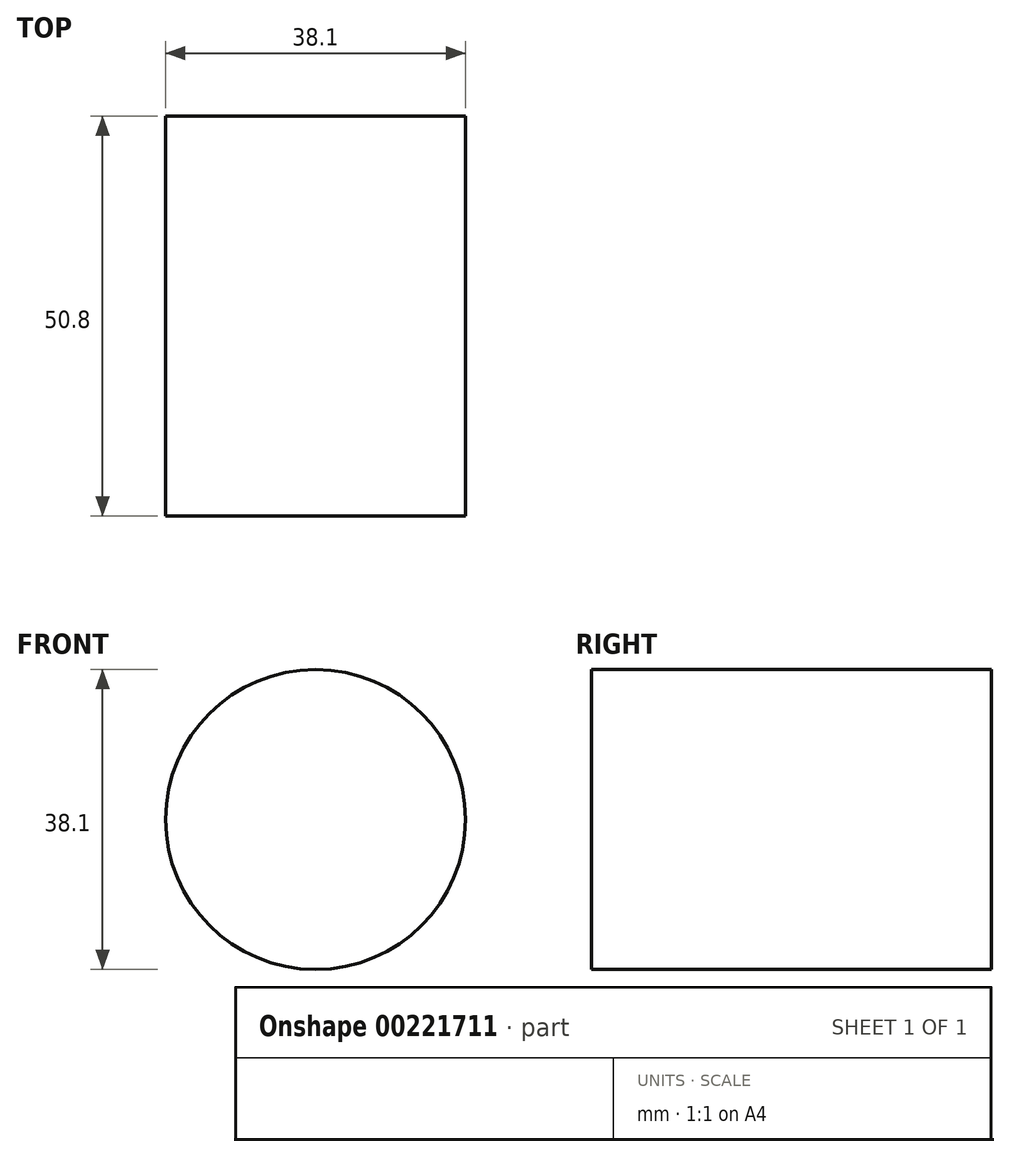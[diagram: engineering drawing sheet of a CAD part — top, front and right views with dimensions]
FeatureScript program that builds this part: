
annotation { "Feature Type Name" : "Feature", "Feature Type Description" : "" }
export const myFeature = defineFeature(function(context is Context, id is Id, definition is map)
    precondition{}
    {
        {
            var Q0;
            Q0=qCreatedBy(makeId("Front.planeOp"),FACE);
            var sketch = newSketch(context, id + "F0", { "sketchPlane" : qUnion([Q0])});
            skCircle(sketch, "E0", {"center": v(0, 0) * mm, "radius": 19.05 * mm});
            skCircle(sketch, "E1.0", {"center": v(0, 0) * mm, "radius": 12.7 * mm});
            skSolve(sketch);
        }
        {
            var Q0;
            Q0=makeQuery(id+"F0.imprint","IMPRINT",FACE,{"disambiguationData":[TD([[makeQuery(id+"F0.imprint","IMPRINT",EDGE,{"derivedFrom":sQuery(id+"F0.wireOp",EDGE,"E0")}),1.0]])]});
            var Q1;
            Q1=makeQuery(id+"F0.imprint","IMPRINT",FACE,{"disambiguationData":[TD([[makeQuery(id+"F0.imprint","IMPRINT",EDGE,{"derivedFrom":sQuery(id+"F0.wireOp",EDGE,"E1.0")}),1.0]])]});
            extrude(context, id + "F1", {"entities" : qUnion([Q0, Q1]), "depth" : 50.8 * mm});
        }
    });
